# Revit family: Sink-Undermount-Kitchen-KOHLER-Undertone-K-3171_1
name_source: partatom
category: Plumbing Fixtures
revit_build: Autodesk Revit 2017 (Build: 20160225_1515(x64)
units: mm (PartAtom-declared; Revit-internal decimal feet)

## family parameters
Cut with Voids When Loaded = No
Host = Face
OmniClass Number = 23.31.13.00
OmniClass Title = Sinks
Part Type = Normal
Room Calculation Point = No
Round Connector Dimension = Use Diameter
Shared = No

## types (2) — shared parameters
ADA Compliant = No
Assembly Code = D2010400
CW Connection = No
Cold Water Inlet = Cold Water Inlet
Date Modified = 09/23/2020
Default Elevation = 36"
Description = 31-1/2inch x 18inch x 9-3/4inch Undermount double-equal bowl kitchen sink
Drain Included = No
Finish = Kohler-Metal-NA-Stainless
HW Connection = No
Height = 9 3/4"
Hot Water Inlet = Hot Water Inlet
Length = 31 1/2"
Manufacturer = KOHLER Co.
Master Format 2014 = 22 41 16
Master Format 2014 Name = Residential Lavatories and Sinks
Material = Premium 18-Gauge Stainless Steel
Product Documentation Link = https://www.us.kohler.com
Product Page URL = http://www.us.kohler.com
URL = https://www.us.kohler.com
Vent Connection = No
Waste Connection = Yes
Waste Water Outlet = Waste Water Outlet
Waste Water Outlet 1 = Waste Water Outlet 1
Waste Water Outlet 2 = Waste Water Outlet 2
WaterSense Certified = No
Width = 18"

## per-type parameters (varying)
| type | Model | Product Name | Sink Rack | Type |
| Without Sink Rack, NA-Stainless | K-3171-NA | Undertone | No | 1 |
| With Sink Rack, NA-Stainless | K-3171-HCF-NA | Undertone Preserve | Yes | 2 |

## geometry (parser evidence)
native form markers: Sweep x4
no freeform markers — native parametric forms only
